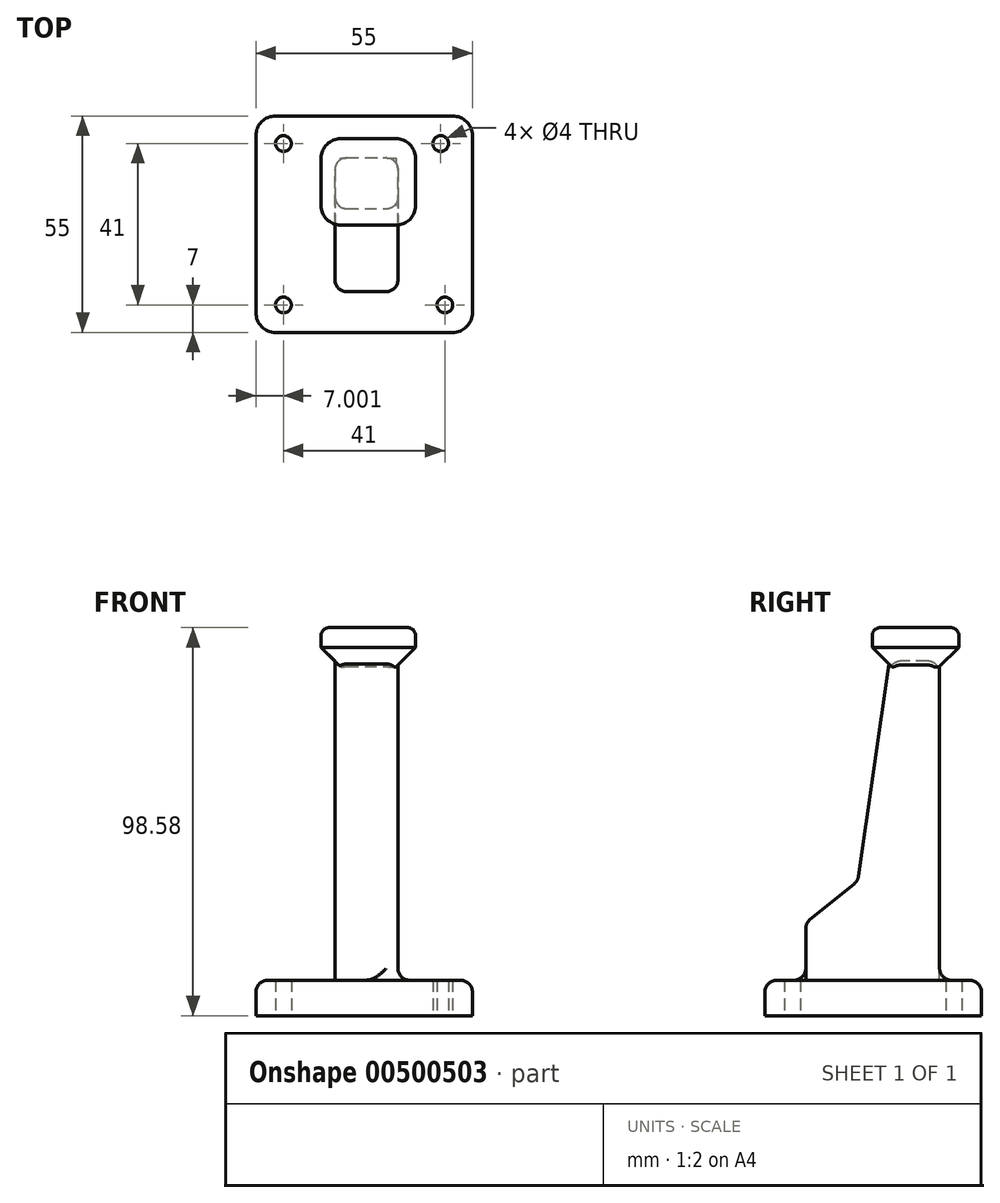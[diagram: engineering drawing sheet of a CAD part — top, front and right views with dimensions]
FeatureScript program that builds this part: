
annotation { "Feature Type Name" : "Feature", "Feature Type Description" : "" }
export const myFeature = defineFeature(function(context is Context, id is Id, definition is map)
    precondition{}
    {
        {
            var Q0;
            Q0=qCreatedBy(makeId("Top.planeOp"),FACE);
            var sketch = newSketch(context, id + "F0", { "sketchPlane" : qUnion([Q0])});
            skLineSegment(sketch, "E0.bottom", {"start": v(-23.07, 26.77) * mm, "end": v(21.93, 26.77) * mm});
            skLineSegment(sketch, "E0.top", {"start": v(-23.07, -28.23) * mm, "end": v(21.93, -28.23) * mm});
            skLineSegment(sketch, "E0.left", {"start": v(-28.07, 21.77) * mm, "end": v(-28.07, -23.23) * mm});
            skLineSegment(sketch, "E0.right", {"start": v(26.93, 21.77) * mm, "end": v(26.93, -23.23) * mm});
            skPoint(sketch, "E1.visualSharp", {"position": v(-28.07, 26.77) * mm});
            skArc(sketch, "E1.filletArc", {"start": v(-23.07, 26.77) * mm, "mid": v(-26.6, 25.3) * mm, "end": v(-28.07, 21.77) * mm});
            skPoint(sketch, "E2.visualSharp", {"position": v(-28.07, -28.23) * mm});
            skArc(sketch, "E2.filletArc", {"start": v(-28.07, -23.23) * mm, "mid": v(-26.6, -26.77) * mm, "end": v(-23.07, -28.23) * mm});
            skPoint(sketch, "E3.visualSharp", {"position": v(26.93, -28.23) * mm});
            skArc(sketch, "E3.filletArc", {"start": v(21.93, -28.23) * mm, "mid": v(25.47, -26.77) * mm, "end": v(26.93, -23.23) * mm});
            skPoint(sketch, "E4.visualSharp", {"position": v(26.93, 26.77) * mm});
            skArc(sketch, "E4.filletArc", {"start": v(26.93, 21.77) * mm, "mid": v(25.47, 25.3) * mm, "end": v(21.93, 26.77) * mm});
            skCircle(sketch, "E5", {"center": v(-21.07, 19.77) * mm, "radius": 2 * mm});
            skCircle(sketch, "E6", {"center": v(18.88, 19.77) * mm, "radius": 2 * mm});
            skCircle(sketch, "E7", {"center": v(-21.07, -21.23) * mm, "radius": 2 * mm});
            skCircle(sketch, "E8", {"center": v(19.93, -21.23) * mm, "radius": 2 * mm});
            skSolve(sketch);
        }
        {
            var Q0;
            Q0 = qSketchRegion(id + "F0", true);
            extrude(context, id + "F1", {"entities" : qUnion([Q0]), "depth" : 9 * mm});
        }
        {
            var Q0;
            Q0=makeQuery(id+"F1.opExtrude","CAP_EDGE",EDGE,{"disambiguationData":[OSD([sQuery(id+"F0.wireOp",EDGE,"E0.right")])],"isStart":false});
            fillet(context, id + "F2", {"entities" : qUnion([Q0]), "radius" : 3 * mm, "tangentPropagation" : true, "allowEdgeOverflow" : false});
        }
        {
            var Q0;
            Q0=qCreatedBy(makeId("Right.planeOp"),FACE);
            var sketch = newSketch(context, id + "F3", { "sketchPlane" : qUnion([Q0])});
            skLineSegment(sketch, "E9", {"start": v(16.14, 8.58) * mm, "end": v(16.14, 88.58) * mm});
            skLineSegment(sketch, "E10", {"start": v(16.14, 88.58) * mm, "end": v(3.14, 88.58) * mm});
            skLineSegment(sketch, "E11", {"start": v(3.14, 88.58) * mm, "end": v(-4.63, 34.26) * mm});
            skLineSegment(sketch, "E12", {"start": v(-4.63, 34.26) * mm, "end": v(-17.86, 23.58) * mm});
            skLineSegment(sketch, "E13", {"start": v(-17.86, 23.58) * mm, "end": v(-17.86, 8.58) * mm});
            skLineSegment(sketch, "E14", {"start": v(-17.86, 8.58) * mm, "end": v(16.14, 8.58) * mm});
            skSolve(sketch);
        }
        {
            var Q0;
            Q0 = qSketchRegion(id + "F3", true);
            extrude(context, id + "F4", {"entities" : qUnion([Q0]), "operationType" : NewBodyOperationType.ADD, "depth" : 8 * mm, "hasSecondDirection" : true, "secondDirectionOppositeDirection" : true, "secondDirectionDepth" : 8 * mm});
        }
        {
            var Q0;
            Q0=makeQuery(id+"F4.opExtrude","CAP_EDGE",EDGE,{"disambiguationData":[OSD([sQuery(id+"F3.wireOp",EDGE,"E11")])],"isStart":true});
            var Q1;
            Q1=makeQuery(id+"F4.opExtrude","CAP_EDGE",EDGE,{"disambiguationData":[OSD([sQuery(id+"F3.wireOp",EDGE,"E12")])],"isStart":true});
            var Q2;
            Q2=makeQuery(id+"F4.opExtrude","CAP_EDGE",EDGE,{"disambiguationData":[OSD([sQuery(id+"F3.wireOp",EDGE,"E13")])],"isStart":true});
            var Q3;
            Q3=makeQuery(id+"F4.opExtrude","CAP_EDGE",EDGE,{"disambiguationData":[OSD([sQuery(id+"F3.wireOp",EDGE,"E9")])],"isStart":true});
            var Q4;
            Q4=makeQuery(id+"F4.opExtrude","CAP_EDGE",EDGE,{"disambiguationData":[OSD([sQuery(id+"F3.wireOp",EDGE,"E11")])],"isStart":false});
            var Q5;
            Q5=makeQuery(id+"F4.opExtrude","CAP_EDGE",EDGE,{"disambiguationData":[OSD([sQuery(id+"F3.wireOp",EDGE,"E12")])],"isStart":false});
            var Q6;
            Q6=makeQuery(id+"F4.opExtrude","CAP_EDGE",EDGE,{"disambiguationData":[OSD([sQuery(id+"F3.wireOp",EDGE,"E13")])],"isStart":false});
            var Q7;
            Q7=makeQuery(id+"F4.opExtrude","CAP_EDGE",EDGE,{"disambiguationData":[OSD([sQuery(id+"F3.wireOp",EDGE,"E9")])],"isStart":false});
            var Q8;
            Q8=makeQuery(id+"F4.boolean.opBoolean","INTERSECT",EDGE,{"derivedFrom":[makeQuery(id+"F1.opExtrude","CAP_FACE",FACE,{"disambiguationData":[OSD([sQuery(id+"F0.wireOp",EDGE,"E0.bottom"),sQuery(id+"F0.wireOp",EDGE,"E0.top"),sQuery(id+"F0.wireOp",EDGE,"E0.left"),sQuery(id+"F0.wireOp",EDGE,"E0.right"),sQuery(id+"F0.wireOp",EDGE,"E1.filletArc"),sQuery(id+"F0.wireOp",EDGE,"E2.filletArc"),sQuery(id+"F0.wireOp",EDGE,"E3.filletArc"),sQuery(id+"F0.wireOp",EDGE,"E4.filletArc"),sQuery(id+"F0.wireOp",EDGE,"E5"),sQuery(id+"F0.wireOp",EDGE,"E6"),sQuery(id+"F0.wireOp",EDGE,"E7"),sQuery(id+"F0.wireOp",EDGE,"E8")])],"isStart":false}),makeQuery(id+"F4.opExtrude","CAP_FACE",FACE,{"disambiguationData":[OSD([sQuery(id+"F3.wireOp",EDGE,"E9"),sQuery(id+"F3.wireOp",EDGE,"E10"),sQuery(id+"F3.wireOp",EDGE,"E11"),sQuery(id+"F3.wireOp",EDGE,"E12"),sQuery(id+"F3.wireOp",EDGE,"E13"),sQuery(id+"F3.wireOp",EDGE,"E14")])],"isStart":false})]});
            var Q9;
            Q9=makeQuery(id+"F4.opExtrude","SWEPT_FACE",FACE,{"disambiguationData":[OSD([sQuery(id+"F3.wireOp",EDGE,"E12")])]});
            fillet(context, id + "F5", {"entities" : qUnion([Q0, Q1, Q2, Q3, Q4, Q5, Q6, Q7, Q8, Q9]), "radius" : 3 * mm, "tangentPropagation" : true, "allowEdgeOverflow" : false});
        }
        {
            var Q0;
            Q0=makeQuery(id+"F4.opExtrude","SWEPT_FACE",FACE,{"disambiguationData":[OSD([sQuery(id+"F3.wireOp",EDGE,"E10")])]});
            cPlane(context, id + "F6", {"entities" : qUnion([Q0]), "cplaneType" : CPlaneType.OFFSET, "offset" : 0 * mm, "width" : 150 * mm, "height" : 150 * mm});
        }
        {
            var Q0;
            Q0=qCreatedBy(id+"F6.planeOp",FACE);
            var sketch = newSketch(context, id + "F7", { "sketchPlane" : qUnion([Q0])});
            skLineSegment(sketch, "E15.bottom", {"start": v(-11.5, 21.03) * mm, "end": v(12.5, 21.03) * mm});
            skLineSegment(sketch, "E15.top", {"start": v(-11.5, -0.97) * mm, "end": v(12.5, -0.97) * mm});
            skLineSegment(sketch, "E15.left", {"start": v(-11.5, 21.03) * mm, "end": v(-11.5, -0.97) * mm});
            skLineSegment(sketch, "E15.right", {"start": v(12.5, 21.03) * mm, "end": v(12.5, -0.97) * mm});
            skSolve(sketch);
        }
        {
            var Q0;
            Q0=makeQuery(id+"F7.imprint","IMPRINT",FACE,{"disambiguationData":[TD([[makeQuery(id+"F7.imprint","IMPRINT",EDGE,{"derivedFrom":sQuery(id+"F7.wireOp",EDGE,"E15.bottom")}),-1.0]])]});
            extrude(context, id + "F8", {"entities" : qUnion([Q0]), "operationType" : NewBodyOperationType.ADD, "depth" : 10 * mm});
        }
        {
            var Q0;
            Q0=makeQuery(id+"F8.opExtrude","SWEPT_EDGE",EDGE,{"disambiguationData":[OSD([sQuery(id+"F7.wireOp",EDGE,"E15.top"),sQuery(id+"F7.wireOp",EDGE,"E15.left")])]});
            var Q1;
            Q1=makeQuery(id+"F8.opExtrude","SWEPT_EDGE",EDGE,{"disambiguationData":[OSD([sQuery(id+"F7.wireOp",EDGE,"E15.bottom"),sQuery(id+"F7.wireOp",EDGE,"E15.left")])]});
            var Q2;
            Q2=makeQuery(id+"F8.opExtrude","SWEPT_EDGE",EDGE,{"disambiguationData":[OSD([sQuery(id+"F7.wireOp",EDGE,"E15.top"),sQuery(id+"F7.wireOp",EDGE,"E15.right")])]});
            var Q3;
            Q3=makeQuery(id+"F8.opExtrude","SWEPT_EDGE",EDGE,{"disambiguationData":[OSD([sQuery(id+"F7.wireOp",EDGE,"E15.bottom"),sQuery(id+"F7.wireOp",EDGE,"E15.right")])]});
            fillet(context, id + "F9", {"entities" : qUnion([Q0, Q1, Q2, Q3]), "radius" : 5 * mm, "tangentPropagation" : true, "allowEdgeOverflow" : false});
        }
        {
            var Q0;
            Q0=makeQuery(id+"F8.opExtrude","CAP_EDGE",EDGE,{"disambiguationData":[OSD([sQuery(id+"F7.wireOp",EDGE,"E15.top")])],"isStart":true});
            chamfer(context, id + "F10", {"entities" : qUnion([Q0]), "width" : 5 * mm, "tangentPropagation" : true});
        }
        {
            var Q0;
            Q0=makeQuery(id+"F8.opExtrude","CAP_FACE",FACE,{"disambiguationData":[OSD([sQuery(id+"F7.wireOp",EDGE,"E15.bottom"),sQuery(id+"F7.wireOp",EDGE,"E15.top"),sQuery(id+"F7.wireOp",EDGE,"E15.left"),sQuery(id+"F7.wireOp",EDGE,"E15.right")])],"isStart":false});
            fillet(context, id + "F11", {"entities" : qUnion([Q0]), "radius" : 2 * mm, "tangentPropagation" : true, "allowEdgeOverflow" : false});
        }
    });
